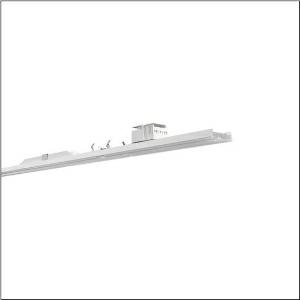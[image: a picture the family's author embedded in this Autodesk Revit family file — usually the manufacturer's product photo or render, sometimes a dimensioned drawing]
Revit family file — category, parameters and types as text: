
# Revit family: licross_r__11_recessed_ho_51tl18dn4c5ld_3d0a
name_source: partatom
category: Lighting Fixtures
units: mm (PartAtom-declared; Revit-internal decimal feet)

## family parameters
Cut with Voids When Loaded = No
Host = Face
Light Source = No
Part Type = Normal
Room Calculation Point = No
Round Connector Dimension = Use Diameter
Shared = No

## types (1)
- --- (1 x LED, 1990 lm, 13.1 W, 4000K)
    Apparent Load = 13 VA
    CIE Flux Codes = 78 94 99 100 100
    Color Rendering = 80
    Color Temperature = 4000K
    Default Elevation = 1800 mm
    Description = Licross® 11 Recessed HOluminaire insert, length: 1.500mm, width: 66mm, height: 67mm, LED rated luminous flux: 12.830lm, light colour: 840, control gear: DALI 2, control gear: ECG DALI, with plug, 6-pole, with phase selection, mains connection: 220..240V, AC/DC, 0/50..60Hz, without changeover relay, for emergency light function, for central battery installations according to DIN EN 60598-2-22, halogen-free wiring, primary optical cover: cover, of PMMA, light emission: direct distribution, protection rating (complete): IP40, insulation class (complete): insulation class I (protective earthing), certification: CE, ENEC, VDE, protection symbol: D if used in an environment without relevant dust loads with corresponding accessories, permissible ambient temperature for indoor applications: -25..+30°C, standard: EN 60598-2-22, reducing of maximum allowable ambient temperature of 5°C with ceiling mounting, corresponds to IFS (International Featured Standards) requirements for safety and quality in the food industry, packaging unit: 1 piece
    Height = 58 mm
    Lamp = 1 x LED
    Lamp Light Flux = 1990 lm
    Lamp Power = 13.1 W
    Lamp count = 1
    Length = 1500 mm
    Luminous efficacy = 152 lm/W
    Manufacturer = Siteco
    ModVariant = No
    Model = 51TL18DN4C5LD
    Mounting Place = Ceiling
    Mounting Type = Pendant
    Number of Poles = 1
    OnlyDefault = Yes
    Power Factor = 1
    Product Name = Licross® 11 Recessed HO
    Product group = luminaire insert
    ProductGroupID = 902
    Protection Class = Protection class I
    Protection Degree = IP 40
    RLX_Detail_Level = 1
    RlxData = <blob elided: 22665 chars, md5=418e5626>
    Socket = socket
    Standby Power = 0 W
    System Light Flux = 1990 lm
    System Power = 13 W
    Type Comments = : DC mode (central or group accumulator) initial emergency light level
    Type Image = l_1266722.jpg
    URL = http://relux.com
    VarID = @adj_134229
    Voltage = 0 V
    Weight = 0.00 kg
    Width = 66 mm

## geometry (parser evidence)
native form markers: Blend x4, Sweep x9
no freeform markers — native parametric forms only
